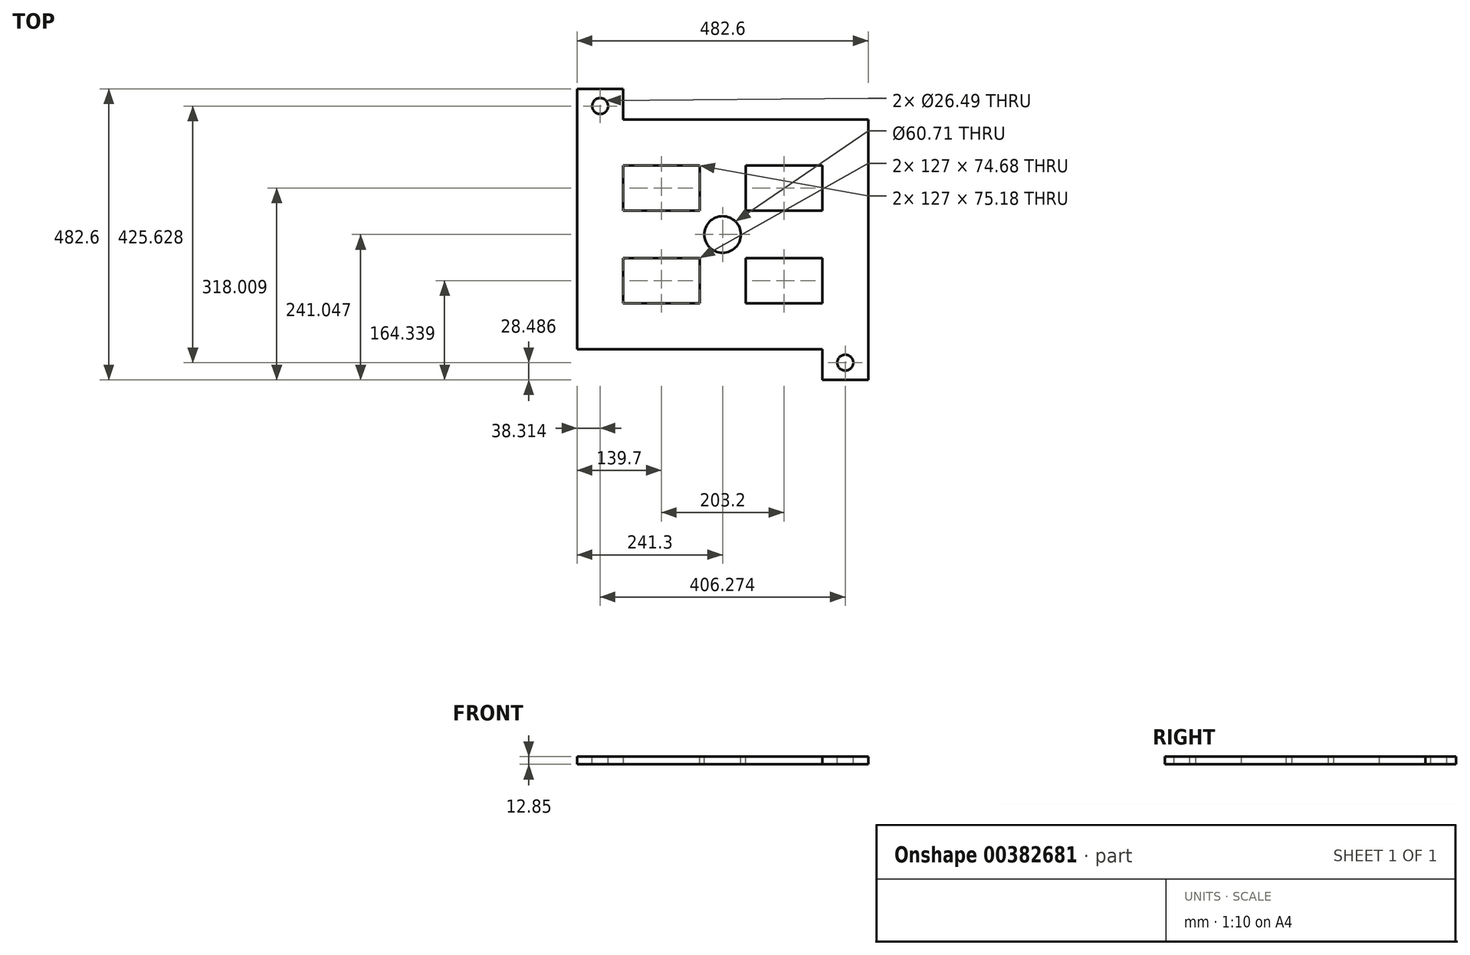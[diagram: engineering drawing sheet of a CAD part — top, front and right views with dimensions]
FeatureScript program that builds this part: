
annotation { "Feature Type Name" : "Feature", "Feature Type Description" : "" }
export const myFeature = defineFeature(function(context is Context, id is Id, definition is map)
    precondition{}
    {
        {
            var Q0;
            Q0=qCreatedBy(makeId("Top.planeOp"),FACE);
            var sketch = newSketch(context, id + "F0", { "sketchPlane" : qUnion([Q0])});
            skLineSegment(sketch, "E0.bottom", {"start": v(0, 0) * mm, "end": v(-482.6, 0) * mm});
            skLineSegment(sketch, "E0.top", {"start": v(0, -482.6) * mm, "end": v(-482.6, -482.6) * mm});
            skLineSegment(sketch, "E0.left", {"start": v(0, 0) * mm, "end": v(0, -482.6) * mm});
            skLineSegment(sketch, "E0.right", {"start": v(-482.6, 0) * mm, "end": v(-482.6, -482.6) * mm});
            skSolve(sketch);
        }
        {
            var Q0;
            Q0=makeQuery(id+"F0.imprint","IMPRINT",FACE,{"disambiguationData":[TD([[makeQuery(id+"F0.imprint","IMPRINT",EDGE,{"derivedFrom":sQuery(id+"F0.wireOp",EDGE,"E0.bottom")}),1.0]])]});
            extrude(context, id + "F1", {"entities" : qUnion([Q0]), "depth" : 12.85 * mm});
        }
        {
            var Q0;
            Q0=makeQuery(id+"F1.opExtrude","SWEPT_FACE",FACE,{"disambiguationData":[OSD([sQuery(id+"F0.wireOp",EDGE,"E0.top")])]});
            var sketch = newSketch(context, id + "F2", { "sketchPlane" : qUnion([Q0])});
            skLineSegment(sketch, "E1.bottom", {"start": v(0, 0) * mm, "end": v(-76.2, 0) * mm});
            skLineSegment(sketch, "E1.top", {"start": v(0, 12.85) * mm, "end": v(-76.2, 12.85) * mm});
            skLineSegment(sketch, "E1.left", {"start": v(0, 0) * mm, "end": v(0, 12.85) * mm});
            skLineSegment(sketch, "E1.right", {"start": v(-76.2, 0) * mm, "end": v(-76.2, 12.85) * mm});
            skLineSegment(sketch, "E2.bottom", {"start": v(-482.6, 12.85) * mm, "end": v(-406.4, 12.85) * mm});
            skLineSegment(sketch, "E2.top", {"start": v(-482.6, 0) * mm, "end": v(-406.4, 0) * mm});
            skLineSegment(sketch, "E2.left", {"start": v(-482.6, 12.85) * mm, "end": v(-482.6, 0) * mm});
            skLineSegment(sketch, "E2.right", {"start": v(-406.4, 12.85) * mm, "end": v(-406.4, 0) * mm});
            skSolve(sketch);
        }
        {
            var Q0;
            {var subQ0=sQuery(id+"F2.wireOp",EDGE,"E1.right");Q0=makeQuery(id+"F2.imprint","IMPRINT",FACE,{"disambiguationData":[TD([[makeQuery(id+"F2.imprint","IMPRINT",EDGE,{"derivedFrom":subQ0}),1.0]])]});}
            var Q1;
            Q1=makeQuery(id+"F2.imprint","IMPRINT",FACE,{"disambiguationData":[TD([[makeQuery(id+"F2.imprint","IMPRINT",EDGE,{"derivedFrom":sQuery(id+"F2.wireOp",EDGE,"E2.bottom")}),1.0]])]});
            extrude(context, id + "F3", {"entities" : qUnion([Q0, Q1]), "operationType" : NewBodyOperationType.REMOVE, "oppositeDirection" : true, "depth" : 50.8 * mm});
        }
        {
            var Q0;
            Q0=makeQuery(id+"F1.opExtrude","SWEPT_FACE",FACE,{"disambiguationData":[OSD([sQuery(id+"F0.wireOp",EDGE,"E0.bottom")])]});
            var sketch = newSketch(context, id + "F4", { "sketchPlane" : qUnion([Q0])});
            skLineSegment(sketch, "E3.bottom", {"start": v(0, 12.85) * mm, "end": v(76.2, 12.85) * mm});
            skLineSegment(sketch, "E3.top", {"start": v(0, 0) * mm, "end": v(76.2, 0) * mm});
            skLineSegment(sketch, "E3.left", {"start": v(0, 12.85) * mm, "end": v(0, 0) * mm});
            skLineSegment(sketch, "E3.right", {"start": v(76.2, 12.85) * mm, "end": v(76.2, 0) * mm});
            skLineSegment(sketch, "E4.bottom", {"start": v(482.6, 12.85) * mm, "end": v(406.4, 12.85) * mm});
            skLineSegment(sketch, "E4.top", {"start": v(482.6, 0) * mm, "end": v(406.4, 0) * mm});
            skLineSegment(sketch, "E4.left", {"start": v(482.6, 12.85) * mm, "end": v(482.6, 0) * mm});
            skLineSegment(sketch, "E4.right", {"start": v(406.4, 12.85) * mm, "end": v(406.4, 0) * mm});
            skSolve(sketch);
        }
        {
            var Q0;
            {var subQ0=sQuery(id+"F4.wireOp",EDGE,"E3.right");Q0=makeQuery(id+"F4.imprint","IMPRINT",FACE,{"disambiguationData":[TD([[makeQuery(id+"F4.imprint","IMPRINT",EDGE,{"derivedFrom":subQ0}),1.0]])]});}
            var Q1;
            Q1=makeQuery(id+"F4.imprint","IMPRINT",FACE,{"disambiguationData":[TD([[makeQuery(id+"F4.imprint","IMPRINT",EDGE,{"derivedFrom":sQuery(id+"F4.wireOp",EDGE,"E3.bottom")}),-1.0]])]});
            extrude(context, id + "F5", {"entities" : qUnion([Q0, Q1]), "operationType" : NewBodyOperationType.REMOVE, "oppositeDirection" : true, "depth" : 50.8 * mm});
        }
        {
            var Q0;
            Q0=makeQuery(id+"F1.opExtrude","CAP_FACE",FACE,{"disambiguationData":[OSD([sQuery(id+"F0.wireOp",EDGE,"E0.bottom"),sQuery(id+"F0.wireOp",EDGE,"E0.top"),sQuery(id+"F0.wireOp",EDGE,"E0.left"),sQuery(id+"F0.wireOp",EDGE,"E0.right")])],"isStart":false});
            var sketch = newSketch(context, id + "F6", { "sketchPlane" : qUnion([Q0])});
            skLineSegment(sketch, "E5.bottom", {"start": v(-406.4, -431.8) * mm, "end": v(-76.2, -431.8) * mm, "construction": true});
            skLineSegment(sketch, "E5.top", {"start": v(-406.4, -355.6) * mm, "end": v(-76.2, -355.6) * mm, "construction": true});
            skLineSegment(sketch, "E5.left", {"start": v(-406.4, -431.8) * mm, "end": v(-406.4, -355.6) * mm, "construction": true});
            skLineSegment(sketch, "E5.right", {"start": v(-76.2, -431.8) * mm, "end": v(-76.2, -355.6) * mm, "construction": true});
            skSolve(sketch);
        }
        {
            var Q0;
            {var subQ0=sQuery(id+"F0.wireOp",EDGE,"E0.top");Q0=makeQuery(id+"F6.imprint","IMPRINT",FACE,{"disambiguationData":[TD([[makeQuery(id+"F6.imprint","IMPRINT",EDGE,{"derivedFrom":makeQuery(id+"F1.opExtrude","CAP_EDGE",EDGE,{"disambiguationData":[OSD([subQ0])],"isStart":false})}),-1.0]])]});}
            var sketch = newSketch(context, id + "F7", { "sketchPlane" : qUnion([Q0])});
            skLineSegment(sketch, "E6.0.0", {"start": v(0, -482.6) * mm, "end": v(0, -50.8) * mm});
            skLineSegment(sketch, "E6.0.1", {"start": v(0, -50.8) * mm, "end": v(-406.4, -50.8) * mm});
            skLineSegment(sketch, "E6.0.2", {"start": v(-406.4, -50.8) * mm, "end": v(-406.4, 0) * mm});
            skLineSegment(sketch, "E6.0.3", {"start": v(-406.4, 0) * mm, "end": v(-482.6, 0) * mm});
            skLineSegment(sketch, "E6.0.4", {"start": v(-482.6, 0) * mm, "end": v(-482.6, -431.8) * mm});
            skLineSegment(sketch, "E6.0.5", {"start": v(-482.6, -431.8) * mm, "end": v(-76.2, -431.8) * mm});
            skLineSegment(sketch, "E6.0.6", {"start": v(-76.2, -431.8) * mm, "end": v(-76.2, -482.6) * mm});
            skLineSegment(sketch, "E6.0.7", {"start": v(-76.2, -482.6) * mm, "end": v(0, -482.6) * mm});
            skLineSegment(sketch, "E7.bottom", {"start": v(-406.4, -50.8) * mm, "end": v(-76.2, -50.8) * mm});
            skLineSegment(sketch, "E7.top", {"start": v(-406.4, -127) * mm, "end": v(-76.2, -127) * mm});
            skLineSegment(sketch, "E7.left", {"start": v(-406.4, -50.8) * mm, "end": v(-406.4, -127) * mm});
            skLineSegment(sketch, "E7.right", {"start": v(-76.2, -50.8) * mm, "end": v(-76.2, -127) * mm});
            skLineSegment(sketch, "E8.0", {"start": v(-406.4, -355.6) * mm, "end": v(-76.2, -355.6) * mm});
            skSolve(sketch);
        }
        {
            var Q0;
            {var subQ0=sQuery(id+"F0.wireOp",EDGE,"E0.top");Q0=makeQuery(id+"F6.imprint","IMPRINT",FACE,{"disambiguationData":[TD([[makeQuery(id+"F6.imprint","IMPRINT",EDGE,{"derivedFrom":makeQuery(id+"F1.opExtrude","CAP_EDGE",EDGE,{"disambiguationData":[OSD([subQ0])],"isStart":false})}),-1.0]])]});}
            var sketch = newSketch(context, id + "F8", { "sketchPlane" : qUnion([Q0])});
            skLineSegment(sketch, "E9.0", {"start": v(-406.4, -355.6) * mm, "end": v(-76.2, -355.6) * mm});
            skLineSegment(sketch, "E10.0", {"start": v(-406.4, -127) * mm, "end": v(-76.2, -127) * mm});
            skLineSegment(sketch, "E11.bottom", {"start": v(-279.4, -355.6) * mm, "end": v(-203.2, -355.6) * mm});
            skLineSegment(sketch, "E11.left", {"start": v(-279.4, -355.6) * mm, "end": v(-279.4, -280.92) * mm});
            skLineSegment(sketch, "E11.right", {"start": v(-203.2, -355.6) * mm, "end": v(-203.2, -280.92) * mm});
            skLineSegment(sketch, "E12.bottom", {"start": v(-279.4, -127) * mm, "end": v(-203.2, -127) * mm});
            skLineSegment(sketch, "E12.top", {"start": v(-279.4, -202.18) * mm, "end": v(-203.2, -202.18) * mm});
            skLineSegment(sketch, "E12.left", {"start": v(-279.4, -127) * mm, "end": v(-279.4, -202.18) * mm});
            skLineSegment(sketch, "E12.right", {"start": v(-203.2, -127) * mm, "end": v(-203.2, -202.18) * mm});
            skLineSegment(sketch, "E13.0.0", {"start": v(0, -482.6) * mm, "end": v(0, -50.8) * mm});
            skLineSegment(sketch, "E13.0.1", {"start": v(0, -50.8) * mm, "end": v(-406.4, -50.8) * mm});
            skLineSegment(sketch, "E13.0.2", {"start": v(-406.4, -50.8) * mm, "end": v(-406.4, 0) * mm});
            skLineSegment(sketch, "E13.0.3", {"start": v(-406.4, 0) * mm, "end": v(-482.6, 0) * mm});
            skLineSegment(sketch, "E13.0.4", {"start": v(-482.6, 0) * mm, "end": v(-482.6, -431.8) * mm});
            skLineSegment(sketch, "E13.0.5", {"start": v(-482.6, -431.8) * mm, "end": v(-76.2, -431.8) * mm});
            skLineSegment(sketch, "E13.0.6", {"start": v(-76.2, -431.8) * mm, "end": v(-76.2, -482.6) * mm});
            skLineSegment(sketch, "E13.0.7", {"start": v(-76.2, -482.6) * mm, "end": v(0, -482.6) * mm});
            skLineSegment(sketch, "E14.0", {"start": v(-406.4, -50.8) * mm, "end": v(-406.4, -127) * mm});
            skLineSegment(sketch, "E15", {"start": v(-406.4, -50.8) * mm, "end": v(-406.4, -431.8) * mm});
            skPoint(sketch, "E16.0", {"position": v(-76.2, -88.9) * mm});
            skLineSegment(sketch, "E17.0", {"start": v(-76.2, -50.8) * mm, "end": v(-76.2, -127) * mm});
            skLineSegment(sketch, "E18", {"start": v(-76.2, -50.8) * mm, "end": v(-76.2, -431.8) * mm});
            skLineSegment(sketch, "E19.left", {"start": v(-406.4, -202.18) * mm, "end": v(-406.4, -280.92) * mm});
            skLineSegment(sketch, "E19.right", {"start": v(-76.2, -202.18) * mm, "end": v(-76.2, -280.92) * mm});
            skLineSegment(sketch, "E20", {"start": v(-279.4, -280.92) * mm, "end": v(-406.4, -280.92) * mm});
            skLineSegment(sketch, "E21", {"start": v(-279.4, -280.92) * mm, "end": v(-76.2, -280.92) * mm});
            skLineSegment(sketch, "E22", {"start": v(-76.2, -202.18) * mm, "end": v(-406.4, -202.18) * mm});
            skSolve(sketch);
        }
        {
            var Q0;
            Q0=makeQuery(id+"F7.imprint","IMPRINT",FACE,{"disambiguationData":[TD([[makeQuery(id+"F7.imprint","IMPRINT",EDGE,{"derivedFrom":sQuery(id+"F7.wireOp",EDGE,"E7.top")}),-1.0]])]});
            var sketch = newSketch(context, id + "F9", { "sketchPlane" : qUnion([Q0])});
            skLineSegment(sketch, "E23.0", {"start": v(-279.4, -355.6) * mm, "end": v(-279.4, -280.92) * mm});
            skLineSegment(sketch, "E24.0", {"start": v(-279.4, -280.92) * mm, "end": v(-406.4, -280.92) * mm});
            skLineSegment(sketch, "E25.0", {"start": v(-406.4, -50.8) * mm, "end": v(-406.4, -431.8) * mm});
            skLineSegment(sketch, "E26.0", {"start": v(-406.4, -355.6) * mm, "end": v(-76.2, -355.6) * mm});
            skLineSegment(sketch, "E27.top", {"start": v(-279.4, -355.6) * mm, "end": v(-406.4, -355.6) * mm});
            skLineSegment(sketch, "E27.left", {"start": v(-279.4, -280.92) * mm, "end": v(-279.4, -355.6) * mm});
            skLineSegment(sketch, "E27.right", {"start": v(-406.4, -280.92) * mm, "end": v(-406.4, -355.6) * mm});
            skLineSegment(sketch, "E28.0", {"start": v(-279.4, -280.92) * mm, "end": v(-76.2, -280.92) * mm});
            skPoint(sketch, "E29.0", {"position": v(-203.2, -318.26) * mm});
            skLineSegment(sketch, "E30.0", {"start": v(-203.2, -355.6) * mm, "end": v(-203.2, -280.92) * mm});
            skLineSegment(sketch, "E31.0", {"start": v(-76.2, -50.8) * mm, "end": v(-76.2, -431.8) * mm});
            skLineSegment(sketch, "E32.bottom", {"start": v(-76.2, -280.92) * mm, "end": v(-203.2, -280.92) * mm});
            skLineSegment(sketch, "E32.top", {"start": v(-76.2, -355.6) * mm, "end": v(-203.2, -355.6) * mm});
            skLineSegment(sketch, "E32.left", {"start": v(-76.2, -280.92) * mm, "end": v(-76.2, -355.6) * mm});
            skLineSegment(sketch, "E32.right", {"start": v(-203.2, -280.92) * mm, "end": v(-203.2, -355.6) * mm});
            skSolve(sketch);
        }
        {
            var Q0;
            {var subQ3=sQuery(id+"F8.wireOp",EDGE,"E11.right");Q0=makeQuery(id+"F8.imprint","IMPRINT",FACE,{"disambiguationData":[TD([[makeQuery(id+"F8.imprint","IMPRINT",EDGE,{"derivedFrom":subQ3}),-1.0]])]});}
            var Q1;
            Q1=makeQuery(id+"F9.imprint","IMPRINT",FACE,{"disambiguationData":[TD([[makeQuery(id+"F9.imprint","IMPRINT",EDGE,{"derivedFrom":sQuery(id+"F9.wireOp",EDGE,"E24.0")}),1.0]])]});
            var Q2;
            {var subQ3=sQuery(id+"F8.wireOp",EDGE,"E12.left");Q2=makeQuery(id+"F8.imprint","IMPRINT",FACE,{"disambiguationData":[TD([[makeQuery(id+"F8.imprint","IMPRINT",EDGE,{"derivedFrom":subQ3}),-1.0]])]});}
            var Q3;
            {var subQ3=sQuery(id+"F8.wireOp",EDGE,"E12.right");Q3=makeQuery(id+"F8.imprint","IMPRINT",FACE,{"disambiguationData":[TD([[makeQuery(id+"F8.imprint","IMPRINT",EDGE,{"derivedFrom":subQ3}),1.0]])]});}
            extrude(context, id + "F10", {"entities" : qUnion([Q0, Q1, Q2, Q3]), "operationType" : NewBodyOperationType.REMOVE, "oppositeDirection" : true, "depth" : 25.4 * mm});
        }
        {
            var Q0;
            {var subQ0=sQuery(id+"F0.wireOp",EDGE,"E0.top");Q0=makeQuery(id+"F6.imprint","IMPRINT",FACE,{"disambiguationData":[TD([[makeQuery(id+"F6.imprint","IMPRINT",EDGE,{"derivedFrom":makeQuery(id+"F1.opExtrude","CAP_EDGE",EDGE,{"disambiguationData":[OSD([subQ0])],"isStart":false})}),-1.0]])]});}
            var sketch = newSketch(context, id + "F11", { "sketchPlane" : qUnion([Q0])});
            skCircle(sketch, "E33", {"center": v(-444.29, -28.49) * mm, "radius": 13.25 * mm});
            skLineSegment(sketch, "E34.0.0", {"start": v(0, -482.6) * mm, "end": v(0, -50.8) * mm});
            skLineSegment(sketch, "E34.0.1", {"start": v(0, -50.8) * mm, "end": v(-406.4, -50.8) * mm});
            skLineSegment(sketch, "E34.0.2", {"start": v(-406.4, -50.8) * mm, "end": v(-406.4, 0) * mm});
            skLineSegment(sketch, "E34.0.3", {"start": v(-406.4, 0) * mm, "end": v(-482.6, 0) * mm});
            skLineSegment(sketch, "E34.0.4", {"start": v(-482.6, 0) * mm, "end": v(-482.6, -431.8) * mm});
            skLineSegment(sketch, "E34.0.5", {"start": v(-482.6, -431.8) * mm, "end": v(-76.2, -431.8) * mm});
            skLineSegment(sketch, "E34.0.6", {"start": v(-76.2, -431.8) * mm, "end": v(-76.2, -482.6) * mm});
            skLineSegment(sketch, "E34.0.7", {"start": v(-76.2, -482.6) * mm, "end": v(0, -482.6) * mm});
            skPoint(sketch, "E35.0", {"position": v(-342.9, -202.18) * mm});
            skLineSegment(sketch, "E36.0", {"start": v(-279.4, -202.18) * mm, "end": v(-406.4, -202.18) * mm});
            skLineSegment(sketch, "E37.0", {"start": v(-279.4, -280.92) * mm, "end": v(-406.4, -280.92) * mm});
            skLineSegment(sketch, "E38.0", {"start": v(-203.2, -280.92) * mm, "end": v(-76.2, -280.92) * mm});
            skLineSegment(sketch, "E39.0", {"start": v(-76.2, -202.18) * mm, "end": v(-203.2, -202.18) * mm});
            skCircle(sketch, "E40", {"center": v(-241.3, -241.55) * mm, "radius": 30.35 * mm});
            skCircle(sketch, "E41", {"center": v(-38.01, -454.11) * mm, "radius": 13.25 * mm});
            skSolve(sketch);
        }
        {
            var Q0;
            Q0=makeQuery(id+"F7.imprint","IMPRINT",FACE,{"disambiguationData":[TD([[makeQuery(id+"F7.imprint","IMPRINT",EDGE,{"derivedFrom":sQuery(id+"F7.wireOp",EDGE,"E7.top")}),-1.0]])]});
            var sketch = newSketch(context, id + "F12", { "sketchPlane" : qUnion([Q0])});
            skCircle(sketch, "E42.0", {"center": v(-444.29, -28.49) * mm, "radius": 13.25 * mm});
            skCircle(sketch, "E43.0", {"center": v(-241.3, -241.55) * mm, "radius": 30.35 * mm});
            skCircle(sketch, "E44.0", {"center": v(-38.01, -454.11) * mm, "radius": 13.25 * mm});
            skSolve(sketch);
        }
        {
            var Q0;
            Q0 = qSketchRegion(id + "F12", true);
            extrude(context, id + "F13", {"entities" : qUnion([Q0]), "operationType" : NewBodyOperationType.REMOVE, "oppositeDirection" : true, "depth" : 25.4 * mm});
        }
    });
